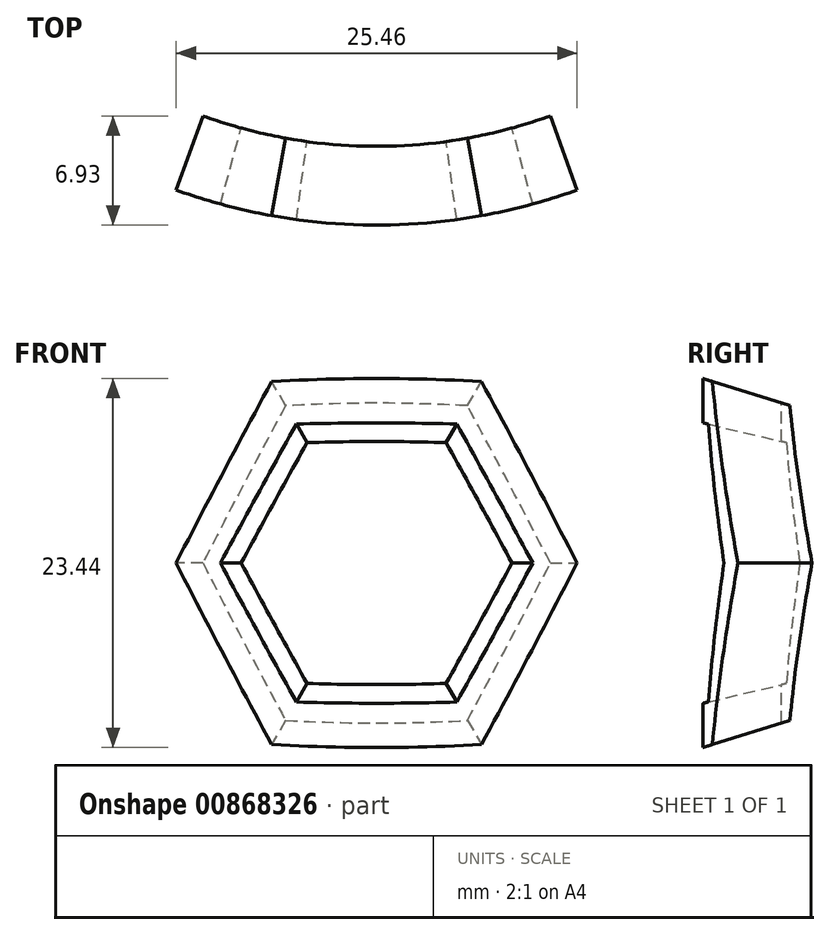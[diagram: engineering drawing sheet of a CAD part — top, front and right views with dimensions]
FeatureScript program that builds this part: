
annotation { "Feature Type Name" : "Feature", "Feature Type Description" : "" }
export const myFeature = defineFeature(function(context is Context, id is Id, definition is map)
    precondition{}
    {
        {
            var Q0;
            Q0=qCreatedBy(makeId("Front.planeOp"),FACE);
            cPlane(context, id + "F0", {"entities" : qUnion([Q0]), "cplaneType" : CPlaneType.OFFSET, "offset" : 40 * mm, "width" : 150 * mm, "height" : 150 * mm});
        }
        {
            var Q0;
            Q0=qCreatedBy(id+"F0.planeOp",FACE);
            var sketch = newSketch(context, id + "F1", { "sketchPlane" : qUnion([Q0])});
            skCircle(sketch, "E0.cCircle", {"center": v(0, 0) * mm, "radius": 12.5 * mm, "construction": true});
            skLineSegment(sketch, "E0.0", {"start": v(7.22, -12.5) * mm, "end": v(-7.22, -12.5) * mm});
            skLineSegment(sketch, "E0.1", {"start": v(-7.22, -12.5) * mm, "end": v(-14.43, 0) * mm});
            skLineSegment(sketch, "E0.2", {"start": v(-14.43, 0) * mm, "end": v(-7.22, 12.5) * mm});
            skLineSegment(sketch, "E0.3", {"start": v(-7.22, 12.5) * mm, "end": v(7.22, 12.5) * mm});
            skLineSegment(sketch, "E0.4", {"start": v(7.22, 12.5) * mm, "end": v(14.43, 0) * mm});
            skLineSegment(sketch, "E0.5", {"start": v(14.43, 0) * mm, "end": v(7.22, -12.5) * mm});
            skPoint(sketch, "E0.0.midPoint", {"position": v(0, -12.5) * mm});
            skSolve(sketch);
        }
        {
            var Q0;
            Q0=qCreatedBy(makeId("Origin.pointOp"),VERTEX);
            var Q1;
            Q1=makeQuery(id+"F1.imprint","IMPRINT",FACE,{"disambiguationData":[TD([[makeQuery(id+"F1.imprint","IMPRINT",EDGE,{"derivedFrom":sQuery(id+"F1.wireOp",EDGE,"E0.0")}),-1.0]])]});
            loft(context, id + "F2", {"sheetProfilesArray" : [{ "sheetProfileEntities" : qUnion([Q0]) }, { "sheetProfileEntities" : qUnion([Q1]) }]});
        }
        {
            var Q0;
            Q0=qCreatedBy(makeId("Front.planeOp"),FACE);
            cPlane(context, id + "F3", {"entities" : qUnion([Q0]), "cplaneType" : CPlaneType.OFFSET, "offset" : 0.1 * mm, "width" : 150 * mm, "height" : 150 * mm});
        }
        {
            var Q0;
            Q0=qCreatedBy(id+"F0.planeOp",FACE);
            var sketch = newSketch(context, id + "F4", { "sketchPlane" : qUnion([Q0])});
            skCircle(sketch, "E1.cCircle", {"center": v(0, 0) * mm, "radius": 9.5 * mm, "construction": true});
            skLineSegment(sketch, "E1.0", {"start": v(5.48, -9.5) * mm, "end": v(-5.48, -9.5) * mm});
            skLineSegment(sketch, "E1.1", {"start": v(-5.48, -9.5) * mm, "end": v(-10.97, 0) * mm});
            skLineSegment(sketch, "E1.2", {"start": v(-10.97, 0) * mm, "end": v(-5.48, 9.5) * mm});
            skLineSegment(sketch, "E1.3", {"start": v(-5.48, 9.5) * mm, "end": v(5.48, 9.5) * mm});
            skLineSegment(sketch, "E1.4", {"start": v(5.48, 9.5) * mm, "end": v(10.97, 0) * mm});
            skLineSegment(sketch, "E1.5", {"start": v(10.97, 0) * mm, "end": v(5.48, -9.5) * mm});
            skPoint(sketch, "E1.0.midPoint", {"position": v(0, -9.5) * mm});
            skSolve(sketch);
        }
        {
            var Q0;
            Q0=qCreatedBy(id+"F3.planeOp",FACE);
            var sketch = newSketch(context, id + "F5", { "sketchPlane" : qUnion([Q0])});
            skLineSegment(sketch, "E2", {"start": v(-0.02, 0.03) * mm, "end": v(-0.04, 0) * mm});
            skLineSegment(sketch, "E3", {"start": v(0.02, 0.03) * mm, "end": v(-0.02, 0.03) * mm});
            skLineSegment(sketch, "E4", {"start": v(-0.04, 0) * mm, "end": v(-0.02, -0.03) * mm});
            skLineSegment(sketch, "E5", {"start": v(0.04, 0) * mm, "end": v(0.02, 0.03) * mm});
            skLineSegment(sketch, "E6", {"start": v(0.02, -0.03) * mm, "end": v(0.04, 0) * mm});
            skLineSegment(sketch, "E7", {"start": v(-0.02, -0.03) * mm, "end": v(0.02, -0.03) * mm});
            skSolve(sketch);
        }
        {
            var Q1;
            Q1=makeQuery(id+"F4.imprint","IMPRINT",FACE,{"disambiguationData":[TD([[makeQuery(id+"F4.imprint","IMPRINT",EDGE,{"derivedFrom":sQuery(id+"F4.wireOp",EDGE,"E1.0")}),-1.0]])]});
            var Q2;
            Q2=makeQuery(id+"F5.imprint","IMPRINT",FACE,{"disambiguationData":[TD([[makeQuery(id+"F5.imprint","IMPRINT",EDGE,{"derivedFrom":sQuery(id+"F5.wireOp",EDGE,"E2")}),1.0]])]});
            loft(context, id + "F6", {"operationType" : NewBodyOperationType.REMOVE, "sheetProfilesArray" : [{ "sheetProfileEntities" : qUnion([Q1]) }, { "sheetProfileEntities" : qUnion([Q2]) }]});
        }
        {
            var Q0;
            Q0=qCreatedBy(makeId("Top.planeOp"),FACE);
            var sketch = newSketch(context, id + "F7", { "sketchPlane" : qUnion([Q0])});
            skCircle(sketch, "E8", {"center": v(0, 0) * mm, "radius": 37.5 * mm});
            skCircle(sketch, "E9", {"center": v(0, 0) * mm, "radius": 32.5 * mm});
            skSolve(sketch);
        }
        {
            var Q0;
            Q0=makeQuery(id+"F7.imprint","IMPRINT",FACE,{"disambiguationData":[TD([[makeQuery(id+"F7.imprint","IMPRINT",EDGE,{"derivedFrom":sQuery(id+"F7.wireOp",EDGE,"E8")}),1.0]])]});
            extrude(context, id + "F8", {"entities" : qUnion([Q0]), "operationType" : NewBodyOperationType.INTERSECT, "endBound" : BoundingType.SYMMETRIC, "oppositeDirection" : true, "depth" : 50 * mm, "offsetDistance" : 25 * mm});
        }
    });
